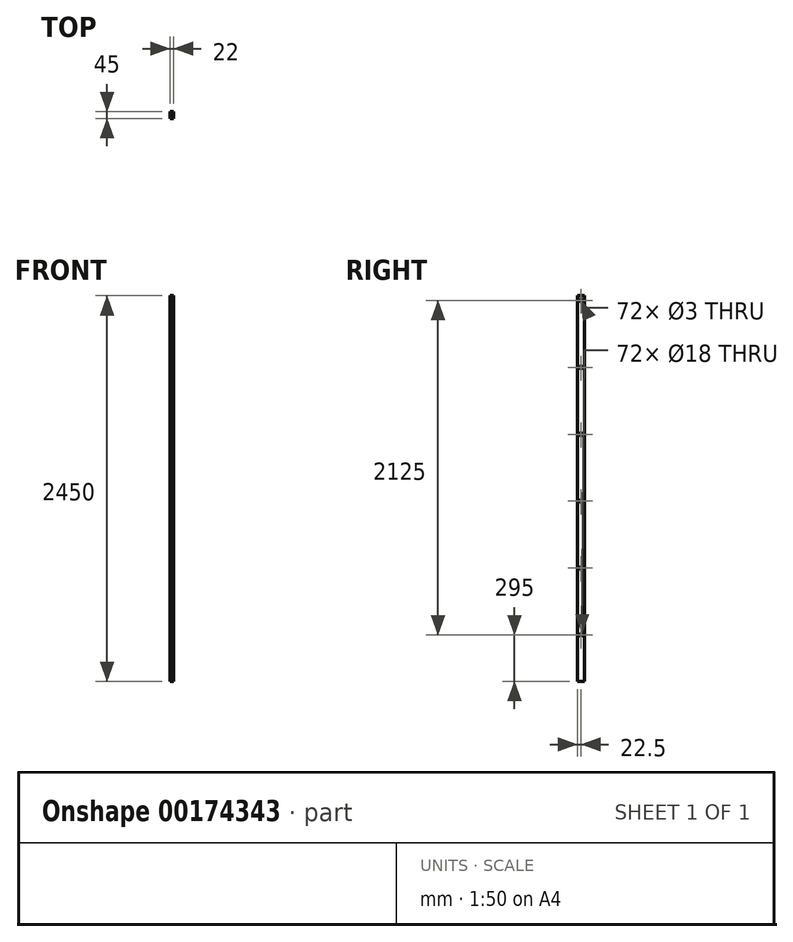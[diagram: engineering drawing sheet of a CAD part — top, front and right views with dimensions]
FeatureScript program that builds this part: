
annotation { "Feature Type Name" : "Feature", "Feature Type Description" : "" }
export const myFeature = defineFeature(function(context is Context, id is Id, definition is map)
    precondition{}
    {
        {
            var Q0;
            Q0=qCreatedBy(makeId("Front.planeOp"),FACE);
            var sketch = newSketch(context, id + "F0", { "sketchPlane" : qUnion([Q0])});
            skLineSegment(sketch, "E0.bottom", {"start": v(-11, 1225) * mm, "end": v(11, 1225) * mm});
            skLineSegment(sketch, "E0.top", {"start": v(-11, -1225) * mm, "end": v(11, -1225) * mm});
            skLineSegment(sketch, "E0.left", {"start": v(-11, 1225) * mm, "end": v(-11, -1225) * mm});
            skLineSegment(sketch, "E0.right", {"start": v(11, 1225) * mm, "end": v(11, -1225) * mm});
            skPoint(sketch, "E0.middle", {"position": v(0, 0) * mm});
            skSolve(sketch);
        }
        {
            var Q0;
            Q0=makeQuery(id+"F0.imprint","IMPRINT",FACE,{"disambiguationData":[TD([[makeQuery(id+"F0.imprint","IMPRINT",EDGE,{"derivedFrom":sQuery(id+"F0.wireOp",EDGE,"E0.bottom")}),-1.0]])]});
            extrude(context, id + "F1", {"entities" : qUnion([Q0]), "depth" : 45 * mm});
        }
        {
            var Q0;
            Q0=makeQuery(id+"F1.opExtrude","SWEPT_FACE",FACE,{"disambiguationData":[OSD([sQuery(id+"F0.wireOp",EDGE,"E0.right")])]});
            var sketch = newSketch(context, id + "F2", { "sketchPlane" : qUnion([Q0])});
            skPoint(sketch, "E1", {"position": v(-22.5, 1195) * mm});
            skPoint(sketch, "E1.positionSnap0", {"position": v(-22.5, 1225) * mm});
            skPoint(sketch, "E2", {"position": v(-22.5, 770) * mm});
            skPoint(sketch, "E3", {"position": v(-22.5, 345) * mm});
            skPoint(sketch, "E4", {"position": v(-22.5, -80) * mm});
            skPoint(sketch, "E5", {"position": v(-22.5, -930) * mm});
            skPoint(sketch, "E6", {"position": v(-22.5, -505) * mm});
            skSolve(sketch);
        }
        {
            var Q0;
            Q0=sQuery(id+"F2.wireOp",VERTEX,"E1");
            var Q1;
            Q1=sQuery(id+"F2.wireOp",VERTEX,"E2");
            var Q2;
            Q2=sQuery(id+"F2.wireOp",VERTEX,"E3");
            var Q3;
            Q3=sQuery(id+"F2.wireOp",VERTEX,"E4");
            var Q4;
            Q4=sQuery(id+"F2.wireOp",VERTEX,"E6");
            var Q5;
            Q5=sQuery(id+"F2.wireOp",VERTEX,"E5");
            var Q6;
            Q6=makeQuery(id+"F1.opExtrude","SWEPT_BODY",BODY,{"disambiguationData":[OSD([sQuery(id+"F0.wireOp",EDGE,"E0.bottom"),sQuery(id+"F0.wireOp",EDGE,"E0.top"),sQuery(id+"F0.wireOp",EDGE,"E0.left"),sQuery(id+"F0.wireOp",EDGE,"E0.right")])]});
            hole(context, id + "F3", {"style" : HoleStyle.SIMPLE, "endStyle" : HoleEndStyle.THROUGH, "holeDiameter" : 3 * mm, "startFromSketch" : true, "locations" : qUnion([Q0, Q1, Q2, Q3, Q4, Q5]), "scope" : qUnion([Q6]), "isTappedThrough" : true});
        }
        {
            var Q0;
            Q0=sQuery(id+"F2.wireOp",VERTEX,"E1");
            var Q1;
            Q1=sQuery(id+"F2.wireOp",VERTEX,"E2");
            var Q2;
            Q2=sQuery(id+"F2.wireOp",VERTEX,"E3");
            var Q3;
            Q3=sQuery(id+"F2.wireOp",VERTEX,"E4");
            var Q4;
            Q4=sQuery(id+"F2.wireOp",VERTEX,"E6");
            var Q5;
            Q5=sQuery(id+"F2.wireOp",VERTEX,"E5");
            var Q6;
            Q6=makeQuery(id+"F1.opExtrude","SWEPT_BODY",BODY,{"disambiguationData":[OSD([sQuery(id+"F0.wireOp",EDGE,"E0.bottom"),sQuery(id+"F0.wireOp",EDGE,"E0.top"),sQuery(id+"F0.wireOp",EDGE,"E0.left"),sQuery(id+"F0.wireOp",EDGE,"E0.right")])]});
            hole(context, id + "F4", {"style" : HoleStyle.SIMPLE, "endStyle" : HoleEndStyle.BLIND, "holeDiameter" : 18 * mm, "holeDepth" : 15 * mm, "startFromSketch" : true, "locations" : qUnion([Q0, Q1, Q2, Q3, Q4, Q5]), "scope" : qUnion([Q6])});
        }
    });
